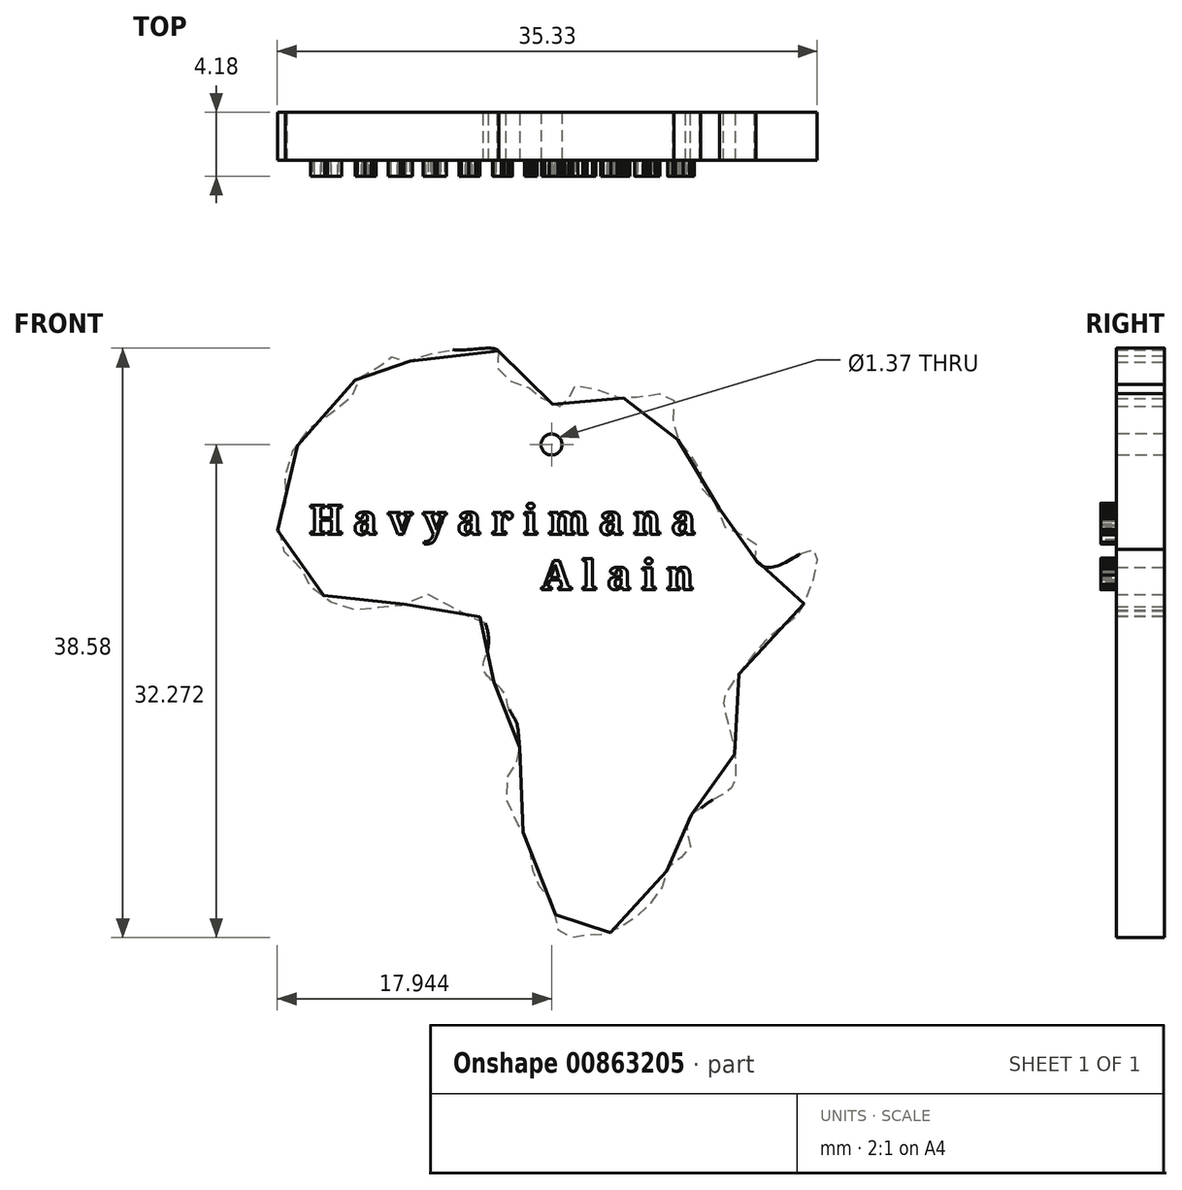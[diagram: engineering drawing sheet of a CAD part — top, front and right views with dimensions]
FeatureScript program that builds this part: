
annotation { "Feature Type Name" : "Feature", "Feature Type Description" : "" }
export const myFeature = defineFeature(function(context is Context, id is Id, definition is map)
    precondition{}
    {
        {
            var Q0;
            Q0=qCreatedBy(makeId("Front.planeOp"),FACE);
            var sketch = newSketch(context, id + "F0", { "sketchPlane" : qUnion([Q0])});
            skPoint(sketch, "E0.44.internal.snap0", {"position": v(-3.76, 22.11) * mm});
            skFitSpline(sketch, "E0", {"points": [v(-7.04, 20.7) * mm, v(-7.04, 19.31) * mm, v(-5.24, 18.4) * mm, v(-4.47, 17.82) * mm, v(-2.85, 17.1) * mm, v(-2.35, 17.82) * mm, v(-1.9, 18.5) * mm, v(0.62, 17.73) * mm, v(2.24, 17.73) * mm, v(4.31, 17.73) * mm, v(4.4, 15.98) * mm, v(5.35, 14.04) * mm, v(6.2, 12.87) * mm, v(6.2, 11.79) * mm, v(7.37, 10.53) * mm, v(7.46, 9.72) * mm, v(8.27, 8.9) * mm, v(9.8, 8.19) * mm, v(9.71, 7.33) * mm, v(10.89, 6.57) * mm, v(13.68, 7.7) * mm, v(12.69, 3.68) * mm, v(11.56, 2.7) * mm, v(9.76, 0.98) * mm, v(8.68, -0.46) * mm, v(7.78, -1.86) * mm, v(7.78, -2.8) * mm, v(8.27, -4.7) * mm, v(8.5, -6.63) * mm, v(8.23, -7.9) * mm, v(7.06, -8.61) * mm, v(5.66, -9.6) * mm, v(5.26, -9.92) * mm, v(5.44, -11.13) * mm, v(5.4, -12.12) * mm, v(4.22, -12.84) * mm, v(3.73, -14.24) * mm, v(2.69, -15.68) * mm, v(1.56, -16.63) * mm, v(0, -17.44) * mm, v(-1.23, -17.53) * mm, v(-2.35, -17.66) * mm, v(-3.16, -17.08) * mm, v(-3.3, -16.18) * mm, v(-3.76, -14.92) * mm, v(-4.65, -13.88) * mm, v(-5.01, -11.58) * mm, v(-6.36, -9.1) * mm, v(-6.27, -6.76) * mm, v(-5.69, -5.95) * mm, v(-5.69, -4.78) * mm, v(-5.87, -3.57) * mm, v(-6.36, -2.67) * mm, v(-6.63, -1.72) * mm, v(-7.53, -0.77) * mm, v(-8.03, 0) * mm, v(-7.76, 1.12) * mm, v(-7.76, 2.47) * mm, v(-8.3, 3.32) * mm, v(-9.56, 3.41) * mm, v(-10.73, 4.5) * mm, v(-12.13, 4.67) * mm, v(-14.15, 3.77) * mm, v(-15.28, 4) * mm, v(-17.04, 3.73) * mm, v(-18.61, 4.8) * mm, v(-19.65, 5.57) * mm, v(-19.87, 6.43) * mm, v(-21.27, 7.87) * mm, v(-21.31, 9.85) * mm, v(-20.86, 11.25) * mm, v(-20.95, 13.23) * mm, v(-20, 14.76) * mm, v(-18.59, 16.45) * mm, v(-16.74, 17.34) * mm, v(-16.42, 18.8) * mm, v(-15.07, 19.33) * mm, v(-14.47, 20.32) * mm, v(-13.97, 20.32) * mm, v(-13.6, 20.05) * mm, v(-12.38, 20.16) * mm, v(-10.94, 20.73) * mm, v(-8.94, 20.8) * mm, v(-7.04, 20.7) * mm]});
            skSolve(sketch);
        }
        {
            var Q0;
            Q0 = qSketchRegion(id + "F0", true);
            extrude(context, id + "F1", {"entities" : qUnion([Q0]), "depth" : 3.14 * mm, "offsetDistance" : 25.4 * mm});
        }
        {
            var Q0;
            Q0=makeQuery(id+"F1.opExtrude","CAP_FACE",FACE,{"disambiguationData":[OSD([sQuery(id+"F0.wireOp",EDGE,"E0")])],"isStart":false});
            var sketch = newSketch(context, id + "F2", { "sketchPlane" : qUnion([Q0])});
            skText(sketch, "E1", { "text": "H a v y a r i m a n a\n                      A l a i n", "fontName": "NotoSerif-Bold.ttf"});
            const initialGuessF2  = {"E1": [-0.0194, 0.00872, 1, 0, 0.00191]};
            skSetInitialGuess(sketch, initialGuessF2);
            skSolve(sketch);
        }
        {
            var Q0;
            Q0 = qSketchRegion(id + "F2", true);
            extrude(context, id + "F3", {"entities" : qUnion([Q0]), "operationType" : NewBodyOperationType.ADD, "depth" : 1.04 * mm, "offsetDistance" : 25.4 * mm});
        }
        {
            var Q0;
            {var subQ0=sQuery(id+"F0.wireOp",EDGE,"E0");Q0=makeQuery(id+"F3.boolean.opBoolean","SPLIT",FACE,{"disambiguationData":[TD([makeQuery(id+"F1.opExtrude","SWEPT_FACE",FACE,{"disambiguationData":[OSD([subQ0])]})])],"derivedFrom":makeQuery(id+"F1.opExtrude","CAP_FACE",FACE,{"disambiguationData":[OSD([subQ0])],"isStart":false})});}
            var sketch = newSketch(context, id + "F4", { "sketchPlane" : qUnion([Q0])});
            skCircle(sketch, "E2", {"center": v(-3.56, 14.6) * mm, "radius": 0.69 * mm});
            skSolve(sketch);
        }
        {
            var Q0;
            Q0 = qSketchRegion(id + "F4", true);
            extrude(context, id + "F5", {"entities" : qUnion([Q0]), "operationType" : NewBodyOperationType.REMOVE, "oppositeDirection" : true, "depth" : 25.4 * mm, "offsetDistance" : 25.4 * mm});
        }
    });
